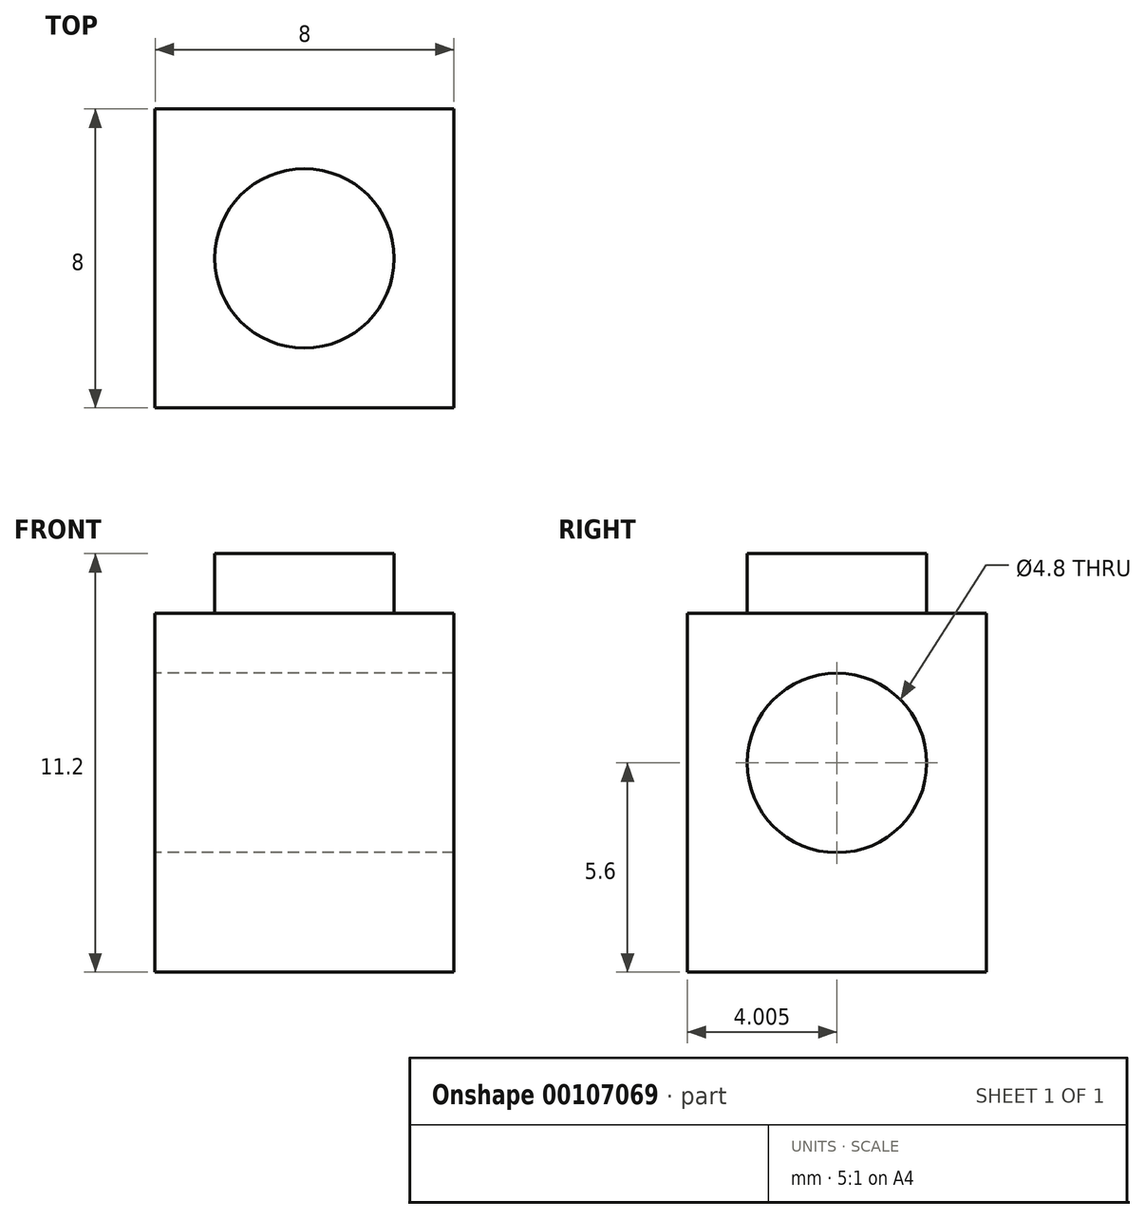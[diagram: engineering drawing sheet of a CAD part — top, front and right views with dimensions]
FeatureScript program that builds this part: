
annotation { "Feature Type Name" : "Feature", "Feature Type Description" : "" }
export const myFeature = defineFeature(function(context is Context, id is Id, definition is map)
    precondition{}
    {
        {
            var Q0;
            Q0=qCreatedBy(makeId("Top.planeOp"),FACE);
            var sketch = newSketch(context, id + "F0", { "sketchPlane" : qUnion([Q0])});
            skLineSegment(sketch, "E0.bottom", {"start": v(-41.67, 46.26) * mm, "end": v(-33.67, 46.26) * mm});
            skLineSegment(sketch, "E0.top", {"start": v(-41.67, 38.26) * mm, "end": v(-33.67, 38.26) * mm});
            skLineSegment(sketch, "E0.left", {"start": v(-41.67, 46.26) * mm, "end": v(-41.67, 38.26) * mm});
            skLineSegment(sketch, "E0.right", {"start": v(-33.67, 46.26) * mm, "end": v(-33.67, 38.26) * mm});
            skSolve(sketch);
        }
        {
            var Q0;
            Q0=makeQuery(id+"F0.imprint","IMPRINT",FACE,{"disambiguationData":[TD([[makeQuery(id+"F0.imprint","IMPRINT",EDGE,{"derivedFrom":sQuery(id+"F0.wireOp",EDGE,"E0.bottom")}),-1.0]])]});
            extrude(context, id + "F1", {"entities" : qUnion([Q0]), "depth" : 9.6 * mm});
        }
        {
            var Q0;
            Q0=makeQuery(id+"F1.opExtrude","SWEPT_FACE",FACE,{"disambiguationData":[OSD([sQuery(id+"F0.wireOp",EDGE,"E0.left")])]});
            var sketch = newSketch(context, id + "F2", { "sketchPlane" : qUnion([Q0])});
            skLineSegment(sketch, "E1", {"start": v(-42.26, 0) * mm, "end": v(-42.26, 5.6) * mm, "construction": true});
            skCircle(sketch, "E2", {"center": v(-42.26, 5.6) * mm, "radius": 2.4 * mm});
            skSolve(sketch);
        }
        {
            var Q0;
            Q0 = qSketchRegion(id + "F2", true);
            extrude(context, id + "F3", {"entities" : qUnion([Q0]), "operationType" : NewBodyOperationType.REMOVE, "oppositeDirection" : true, "depth" : 25 * mm});
        }
        {
            var Q0;
            Q0=makeQuery(id+"F1.opExtrude","CAP_FACE",FACE,{"disambiguationData":[OSD([sQuery(id+"F0.wireOp",EDGE,"E0.bottom"),sQuery(id+"F0.wireOp",EDGE,"E0.top"),sQuery(id+"F0.wireOp",EDGE,"E0.left"),sQuery(id+"F0.wireOp",EDGE,"E0.right")])],"isStart":false});
            var sketch = newSketch(context, id + "F4", { "sketchPlane" : qUnion([Q0])});
            skLineSegment(sketch, "E3", {"start": v(-37.67, 38.26) * mm, "end": v(-37.67, 42.26) * mm, "construction": true});
            skCircle(sketch, "E4", {"center": v(-37.67, 42.26) * mm, "radius": 2.4 * mm});
            skSolve(sketch);
        }
        {
            var Q0;
            Q0 = qSketchRegion(id + "F4", true);
            extrude(context, id + "F5", {"entities" : qUnion([Q0]), "operationType" : NewBodyOperationType.ADD, "depth" : 1.6 * mm});
        }
    });
